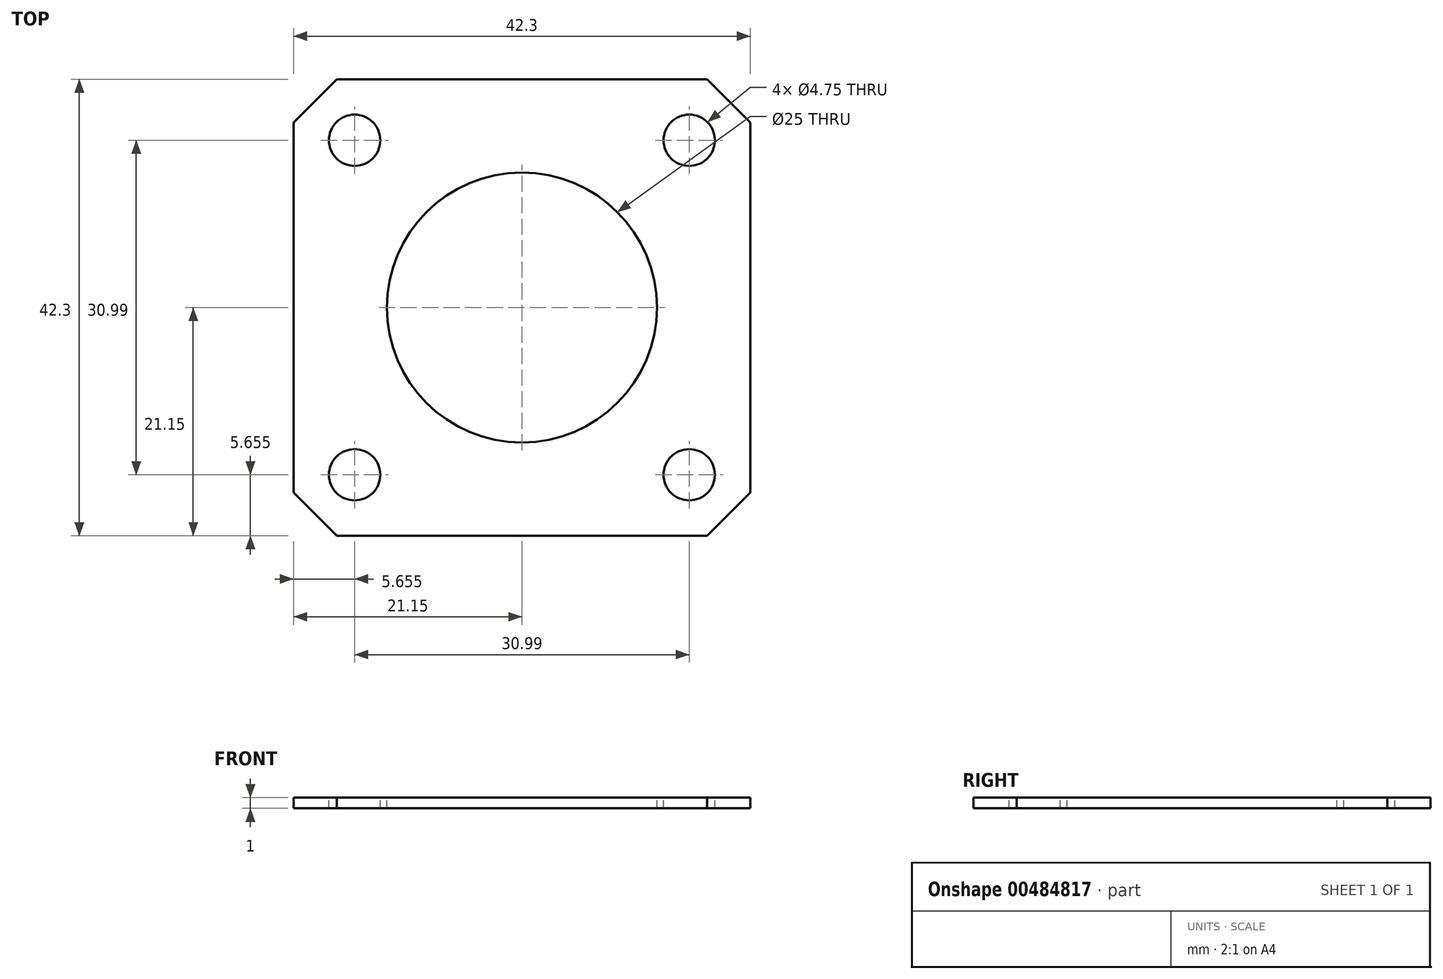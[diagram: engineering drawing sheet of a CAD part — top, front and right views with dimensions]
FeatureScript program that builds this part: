
annotation { "Feature Type Name" : "Feature", "Feature Type Description" : "" }
export const myFeature = defineFeature(function(context is Context, id is Id, definition is map)
    precondition{}
    {
        {
            var Q0;
            Q0=qCreatedBy(makeId("Top.planeOp"),FACE);
            var sketch = newSketch(context, id + "F0", { "sketchPlane" : qUnion([Q0])});
            skLineSegment(sketch, "E0", {"start": v(4, 0) * mm, "end": v(38.3, 0) * mm});
            skLineSegment(sketch, "E1", {"start": v(42.3, 4) * mm, "end": v(42.3, 38.3) * mm});
            skLineSegment(sketch, "E2", {"start": v(38.3, 42.3) * mm, "end": v(4, 42.3) * mm});
            skLineSegment(sketch, "E3", {"start": v(0, 38.3) * mm, "end": v(0, 4) * mm});
            skCircle(sketch, "E4", {"center": v(5.66, 5.66) * mm, "radius": 2.38 * mm});
            skLineSegment(sketch, "E5", {"start": v(5.66, 5.66) * mm, "end": v(36.65, 5.66) * mm, "construction": true});
            skLineSegment(sketch, "E6", {"start": v(36.64, 5.66) * mm, "end": v(36.64, 36.65) * mm, "construction": true});
            skCircle(sketch, "E7", {"center": v(36.65, 5.66) * mm, "radius": 2.38 * mm});
            skCircle(sketch, "E8", {"center": v(36.64, 36.65) * mm, "radius": 2.38 * mm});
            skCircle(sketch, "E9", {"center": v(5.65, 36.65) * mm, "radius": 2.38 * mm});
            skLineSegment(sketch, "E10", {"start": v(36.64, 36.65) * mm, "end": v(5.65, 36.65) * mm, "construction": true});
            skPoint(sketch, "E11.endSnap0", {"position": v(21.15, 42.3) * mm});
            skLineSegment(sketch, "E12", {"start": v(21.15, 36.65) * mm, "end": v(21.15, 5.66) * mm, "construction": true});
            skCircle(sketch, "E13", {"center": v(21.15, 21.15) * mm, "radius": 12.5 * mm});
            skLineSegment(sketch, "E14", {"start": v(4, 0) * mm, "end": v(0, 4) * mm});
            skLineSegment(sketch, "E15", {"start": v(42.3, 21.15) * mm, "end": v(0, 21.15) * mm, "construction": true});
            skLineSegment(sketch, "E16.MirrorCS", {"start": v(38.3, 0) * mm, "end": v(42.3, 4) * mm});
            skLineSegment(sketch, "E17.MirrorCS", {"start": v(38.3, 42.3) * mm, "end": v(42.3, 38.3) * mm});
            skLineSegment(sketch, "E18.MirrorCS", {"start": v(4, 42.3) * mm, "end": v(0, 38.3) * mm});
            skSolve(sketch);
        }
        {
            var Q0;
            Q0 = qSketchRegion(id + "F0", true);
            extrude(context, id + "F1", {"entities" : qUnion([Q0]), "oppositeDirection" : true, "depth" : 1 * mm});
        }
    });
